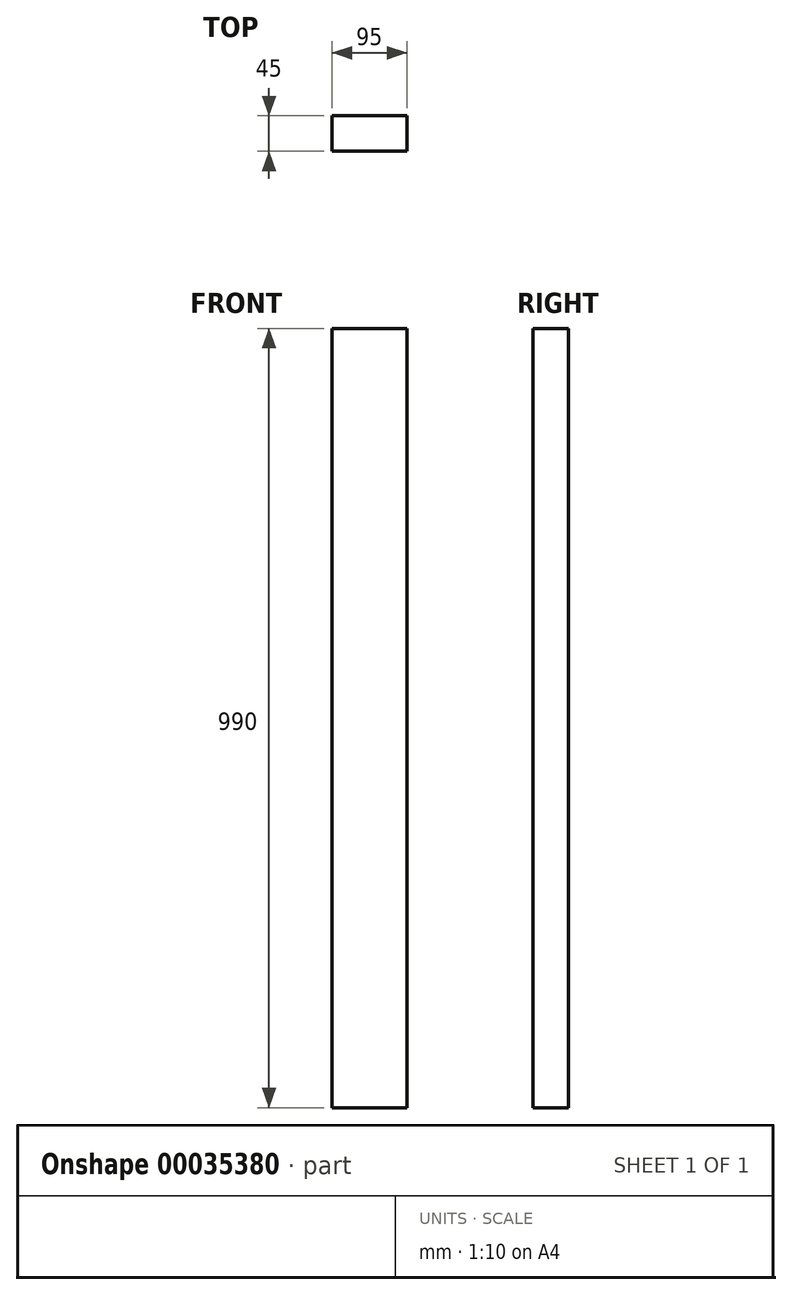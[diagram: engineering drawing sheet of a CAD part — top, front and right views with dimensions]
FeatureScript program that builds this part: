
annotation { "Feature Type Name" : "Feature", "Feature Type Description" : "" }
export const myFeature = defineFeature(function(context is Context, id is Id, definition is map)
    precondition{}
    {
        {
            var Q0;
            Q0=qCreatedBy(makeId("Top.planeOp"),FACE);
            var sketch = newSketch(context, id + "F0", { "sketchPlane" : qUnion([Q0])});
            skLineSegment(sketch, "E0.rect.bottom", {"start": v(47.5, -22.5) * mm, "end": v(-47.5, -22.5) * mm});
            skLineSegment(sketch, "E0.rect.top", {"start": v(47.5, 22.5) * mm, "end": v(-47.5, 22.5) * mm});
            skLineSegment(sketch, "E0.rect.left", {"start": v(47.5, -22.5) * mm, "end": v(47.5, 22.5) * mm});
            skLineSegment(sketch, "E0.rect.right", {"start": v(-47.5, -22.5) * mm, "end": v(-47.5, 22.5) * mm});
            skPoint(sketch, "E0.rect.middle", {"position": v(0, 0) * mm});
            skSolve(sketch);
        }
        {
            var Q0;
            Q0=makeQuery(id+"F0.imprint","IMPRINT",FACE,{"disambiguationData":[TD([[makeQuery(id+"F0.imprint","IMPRINT",EDGE,{"derivedFrom":sQuery(id+"F0.wireOp",EDGE,"E0.rect.bottom")}),-1.0]])]});
            extrude(context, id + "F1", {"entities" : qUnion([Q0]), "depth" : 990 * mm});
        }
    });
